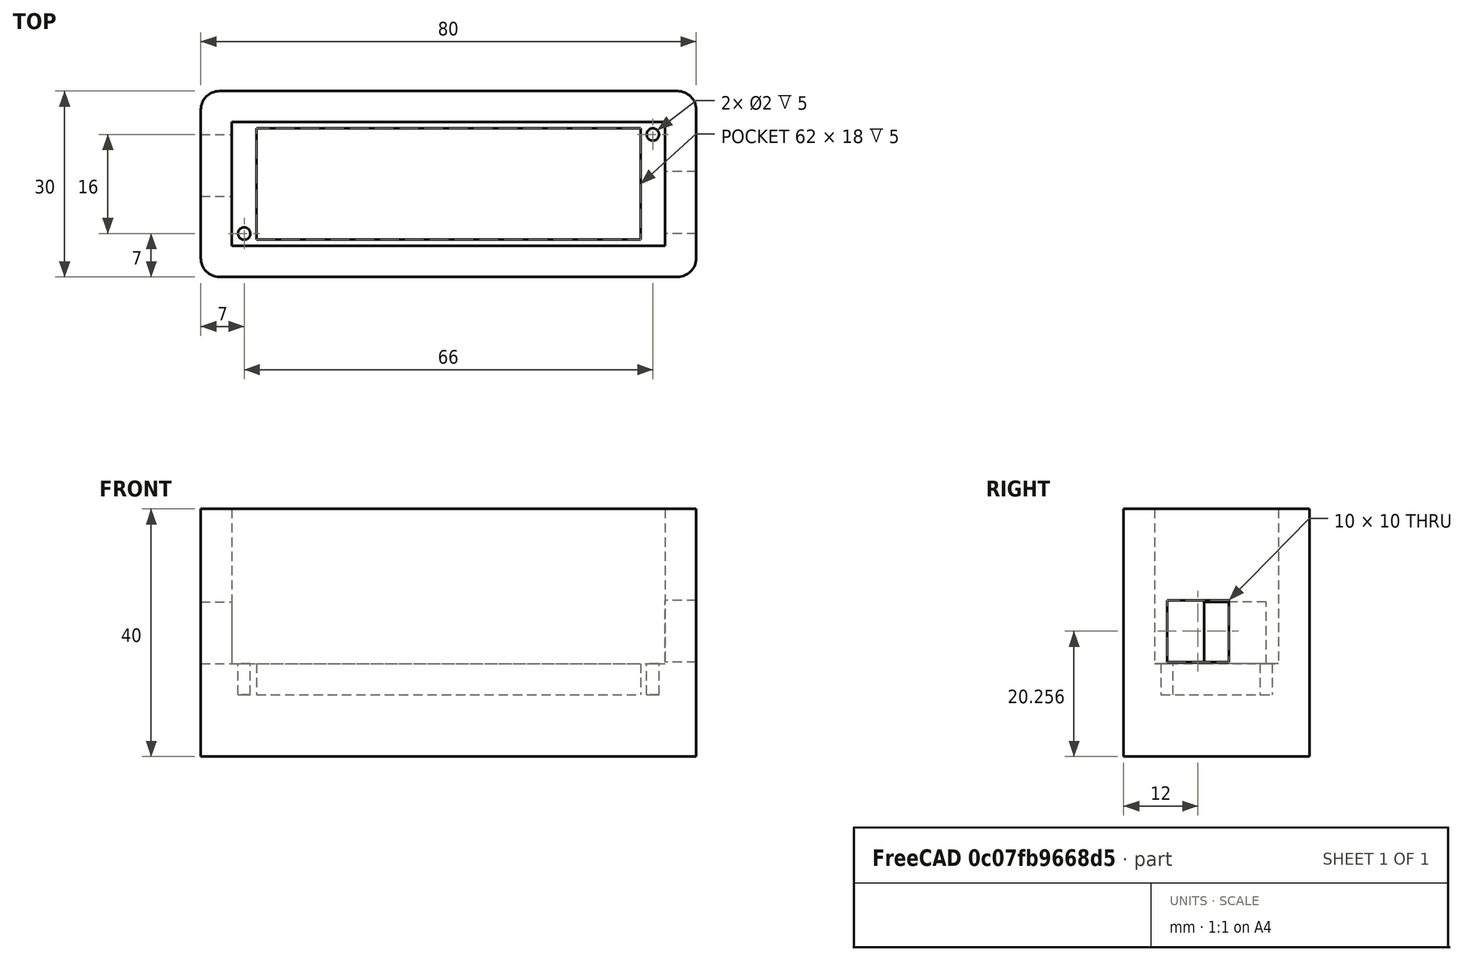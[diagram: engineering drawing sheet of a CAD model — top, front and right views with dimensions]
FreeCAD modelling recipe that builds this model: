
FCSTD DOCUMENT  (FreeCAD 0.20R29603 (Git))
Label: box
License: All rights reserved
LicenseURL: http://en.wikipedia.org/wiki/All_rights_reserved
objects: TechDraw::DrawViewDimension×41, Sketcher::SketchObject×6, PartDesign::Pocket×5, TechDraw::DrawViewSection×3, TechDraw::DrawViewPart×3, TechDraw::DrawSVGTemplate×2, TechDraw::DrawProjGroupItem×2, TechDraw::DrawPage×2, PartDesign::Pad×1, PartDesign::Fillet×1, TechDraw::DrawProjGroup×1, TechDraw::DrawViewDimExtent×1, PartDesign::Body×1
note: 21 computed .brp shape members not serialized (recipe doc carries the construction recipe); baked Part::Feature solids carry a one-line shape summary decoded from their .brp

FEATURE [TechDraw::DrawSVGTemplate] Template
  EditableTexts = Drawing_number=001; FC-SH=001; FC-Title=Box
  Height = 210
  Orientation = 1
  Width = 297
FEATURE [Sketcher::SketchObject] Sketch
  FullyConstrained = true
  MapMode = 5
  Placement = pos=(0,0,0) rot=(0.57735,0.57735,0.57735;2.0944rad)
  Support = -> [YZ_Plane]
  sketch-geometry (4):
    g0: LineSegment StartX=-30 StartY=40 StartZ=0 EndX=0 EndY=40 EndZ=0
    g1: LineSegment StartX=0 StartY=40 StartZ=0 EndX=0 EndY=0 EndZ=0
    g2: LineSegment StartX=0 StartY=0 StartZ=0 EndX=-30 EndY=0 EndZ=0
    g3: LineSegment StartX=-30 StartY=0 StartZ=0 EndX=-30 EndY=40 EndZ=0
  constraints (11):
    c: Coincident(g0,g1)
    c: Coincident(g1,g2)
    c: Coincident(g2,g3)
    c: Coincident(g3,g0)
    c: Horizontal(g0)
    c: Horizontal(g2)
    c: Vertical(g1)
    c: Vertical(g3)
    c: DistanceX(g2,g2) = 30
    c: DistanceY(g1,g1) = 40
    c: Coincident(g1,g-1)
FEATURE [PartDesign::Pad] Pad
  Direction = (1,-2e-16,3e-16)
  Length = 80
  Length2 = 10
  Midplane = true
  Placement = pos=(0,0,0) rot=(0.57735,0.57735,0.57735;2.0944rad)
  Profile = -> Sketch
  ReferenceAxis = -> Sketch [N_Axis]
  Type = 0
FEATURE [Sketcher::SketchObject] Sketch001
  ExternalGeometry = -> [Pad]
  FullyConstrained = true
  MapMode = 5
  Placement = pos=(-1.12e-14,1.76e-14,40) rot=(0,0,-1;1.5708rad)
  Support = -> [Pad]
  sketch-geometry (4):
    g0: LineSegment StartX=5 StartY=35 StartZ=0 EndX=25 EndY=35 EndZ=0
    g1: LineSegment StartX=25 StartY=35 StartZ=0 EndX=25 EndY=-35 EndZ=0
    g2: LineSegment StartX=25 StartY=-35 StartZ=0 EndX=5 EndY=-35 EndZ=0
    g3: LineSegment StartX=5 StartY=-35 StartZ=0 EndX=5 EndY=35 EndZ=0
  constraints (12):
    c: Coincident(g0,g1)
    c: Coincident(g1,g2)
    c: Coincident(g2,g3)
    c: Coincident(g3,g0)
    c: Horizontal(g0)
    c: Horizontal(g2)
    c: Vertical(g1)
    c: Vertical(g3)
    c: DistanceX(g2,g2) = 20
    c: DistanceY(g1,g1) = 70
    c: DistanceX(g1,g-3) = 5
    c: DistanceY(g-3,g1) = 5
FEATURE [PartDesign::Pocket] Pocket
  BaseFeature = -> Pad
  Direction = (4e-16,-6e-16,-1)
  Length = 25
  Length2 = 5
  Placement = pos=(0,0,0) rot=(0.57735,0.57735,0.57735;2.0944rad)
  Profile = -> Sketch001
  ReferenceAxis = -> Sketch001 [N_Axis]
  Type = 0
FEATURE [Sketcher::SketchObject] Sketch002
  ExternalGeometry = -> [Pocket]
  FullyConstrained = true
  MapMode = 5
  Placement = pos=(-6.1e-15,1.06e-14,15) rot=(0,0,-1;1.5708rad)
  Support = -> [Pocket]
  sketch-geometry (4):
    g0: LineSegment StartX=6 StartY=31 StartZ=0 EndX=24 EndY=31 EndZ=0
    g1: LineSegment StartX=24 StartY=31 StartZ=0 EndX=24 EndY=-31 EndZ=0
    g2: LineSegment StartX=24 StartY=-31 StartZ=0 EndX=6 EndY=-31 EndZ=0
    g3: LineSegment StartX=6 StartY=-31 StartZ=0 EndX=6 EndY=31 EndZ=0
  constraints (12):
    c: Coincident(g0,g1)
    c: Coincident(g1,g2)
    c: Coincident(g2,g3)
    c: Coincident(g3,g0)
    c: Horizontal(g0)
    c: Horizontal(g2)
    c: Vertical(g1)
    c: Vertical(g3)
    c: DistanceX(g2,g2) = 18
    c: DistanceY(g1,g1) = 62
    c: DistanceY(g-3,g1) = 4
    c: DistanceX(g1,g-3) = 1
FEATURE [PartDesign::Pocket] Pocket001
  BaseFeature = -> Pocket
  Direction = (7e-16,-8e-16,-1)
  Length = 5
  Length2 = 5
  Placement = pos=(0,0,0) rot=(0.57735,0.57735,0.57735;2.0944rad)
  Profile = -> Sketch002
  ReferenceAxis = -> Sketch002 [N_Axis]
  Type = 0
FEATURE [Sketcher::SketchObject] Sketch003
  ExternalGeometry = -> [Pocket001]
  FullyConstrained = true
  MapMode = 5
  Placement = pos=(-6.1e-15,1.06e-14,15) rot=(0,0,-1;1.5708rad)
  Support = -> [Pocket001]
  expr: Constraints[5] = 1 mm
  sketch-geometry (2):
    g0: Circle CenterX=7 CenterY=33 CenterZ=0 NormalX=0 NormalY=0 NormalZ=1 AngleXU=0 Radius=1
    g1: Circle CenterX=23 CenterY=-33 CenterZ=0 NormalX=0 NormalY=0 NormalZ=1 AngleXU=0 Radius=1
  constraints (6):
    c: DistanceX(g1,g-5) = 1
    c: DistanceY(g1,g-5) = 2
    c: DistanceX(g-6,g0) = 1
    c: DistanceY(g-6,g0) = 2
    c: Radius(g0) = 1
    c: Radius(g1) = 1
FEATURE [PartDesign::Pocket] Pocket002
  BaseFeature = -> Pocket001
  Direction = (1.1e-15,-9e-16,-1)
  Length = 5
  Length2 = 5
  Placement = pos=(0,0,0) rot=(0.57735,0.57735,0.57735;2.0944rad)
  Profile = -> Sketch003
  ReferenceAxis = -> Sketch003 [N_Axis]
  Type = 0
FEATURE [Sketcher::SketchObject] Sketch004
  ExternalGeometry = -> [Pocket002]
  FullyConstrained = true
  MapMode = 5
  Placement = pos=(-40,8.8e-15,-8.8e-15) rot=(0.57735,0.57735,-0.57735;4.18879rad)
  Support = -> [Pocket002]
  sketch-geometry (4):
    g0: LineSegment StartX=-17 StartY=-15 StartZ=0 EndX=-7 EndY=-15 EndZ=0
    g1: LineSegment StartX=-7 StartY=-15 StartZ=0 EndX=-7 EndY=-25 EndZ=0
    g2: LineSegment StartX=-7 StartY=-25 StartZ=0 EndX=-17 EndY=-25 EndZ=0
    g3: LineSegment StartX=-17 StartY=-25 StartZ=0 EndX=-17 EndY=-15 EndZ=0
  constraints (12):
    c: Coincident(g0,g1)
    c: Coincident(g1,g2)
    c: Coincident(g2,g3)
    c: Coincident(g3,g0)
    c: Horizontal(g0)
    c: Horizontal(g2)
    c: Vertical(g1)
    c: Vertical(g3)
    c: Equal(g1,g2)
    c: DistanceX(g2,g2) = 10
    c: DistanceX(g-3,g2) = 13
    c: DistanceY(g-3,g2) = 15
FEATURE [PartDesign::Pocket] Pocket003
  BaseFeature = -> Pocket002
  Direction = (1,-9e-16,8e-16)
  Length = 5
  Length2 = 5
  Placement = pos=(0,0,0) rot=(0.57735,0.57735,0.57735;2.0944rad)
  Profile = -> Sketch004
  ReferenceAxis = -> Sketch004 [N_Axis]
  Type = 0
FEATURE [Sketcher::SketchObject] Sketch005
  ExternalGeometry = -> [Pocket003]
  FullyConstrained = false
  MapMode = 5
  Placement = pos=(40,-9e-15,1.3e-14) rot=(0.57735,0.57735,0.57735;2.0944rad)
  sketch-geometry (4):
    g0: LineSegment StartX=-23 StartY=25.2559 StartZ=0 EndX=-13 EndY=25.2559 EndZ=0
    g1: LineSegment StartX=-13 StartY=25.2559 StartZ=0 EndX=-13 EndY=15.2559 EndZ=0
    g2: LineSegment StartX=-13 StartY=15.2559 StartZ=0 EndX=-23 EndY=15.2559 EndZ=0
    g3: LineSegment StartX=-23 StartY=15.2559 StartZ=0 EndX=-23 EndY=25.2559 EndZ=0
  constraints (11):
    c: Coincident(g0,g1)
    c: Coincident(g1,g2)
    c: Coincident(g2,g3)
    c: Coincident(g3,g0)
    c: Horizontal(g0)
    c: Horizontal(g2)
    c: Vertical(g1)
    c: Vertical(g3)
    c: DistanceX(g2,g2) = 10
    c: Equal(g2,g1)
    c: DistanceX(g-3,g0) = 7
FEATURE [PartDesign::Pocket] Pocket004
  BaseFeature = -> Pocket003
  Direction = (-1,0,0)
  Length = 5
  Length2 = 5
  Placement = pos=(0,0,0) rot=(0.57735,0.57735,0.57735;2.0944rad)
  Profile = -> Sketch005
  ReferenceAxis = -> Sketch005 [N_Axis]
  Type = 0
FEATURE [PartDesign::Fillet] Fillet
  Base = -> Pocket004 [Edge11,Edge18,Edge12,Edge10]
  BaseFeature = -> Pocket004
  Placement = pos=(0,0,0) rot=(0.57735,0.57735,0.57735;2.0944rad)
  Radius = 3
  SupportTransform = false
  UseAllEdges = false
FEATURE [TechDraw::DrawProjGroupItem] ProjItem  label="Front"
  CoarseView = false
  Direction = (0,-1,0)
  Focus = 100
  HardHidden = false
  IsoCount = 0
  IsoHidden = false
  IsoVisible = false
  LockPosition = true
  Perspective = false
  Rotation = 0
  RotationVector = (1,0,0)
  ScaleType = 2
  SeamHidden = false
  SeamVisible = true
  SmoothHidden = false
  SmoothVisible = true
  Source = -> [Fillet]
  Type = 0
  X = 0
  XDirection = (1,0,0)
  Y = 0
FEATURE [TechDraw::DrawProjGroupItem] ProjItem002  label="Top"
  CoarseView = false
  Direction = (0,0,1)
  Focus = 100
  HardHidden = false
  IsoCount = 0
  IsoHidden = false
  IsoVisible = false
  LockPosition = false
  Perspective = false
  Rotation = 0
  RotationVector = (1,0,0)
  ScaleType = 2
  SeamHidden = false
  SeamVisible = true
  SmoothHidden = false
  SmoothVisible = true
  Source = -> [Fillet]
  Type = 4
  X = 0
  XDirection = (1,0,0)
  Y = -70
FEATURE [TechDraw::DrawProjGroup] ProjGroup
  Anchor = -> ProjItem
  AutoDistribute = true
  LockPosition = false
  ProjectionType = 0
  Rotation = 0
  ScaleType = 0
  Source = -> [Fillet]
  Views = -> [ProjItem,ProjItem002]
  X = 82.0393
  Y = 156.709
  spacingX = 20
  spacingY = 30
FEATURE [TechDraw::DrawViewDimExtent] DimExtent
  AngleOverride = false
  Arbitrary = false
  ArbitraryTolerances = false
  CosmeticTags = d0a69e95-236e-45c1-b454-3df11a3e1382 | 03a514d8-6601-4757-9cdd-594276e1f8bd
  DirExtent = 0
  EqualTolerance = true
  ExtensionAngle = 0
  FormatSpec = %.2w
  FormatSpecOverTolerance = %+.2w
  FormatSpecUnderTolerance = %+.2w
  Inverted = false
  LineAngle = 0
  LockPosition = false
  MeasureType = 1
  OverTolerance = 0
  References2D = -> [ProjItem]
  Rotation = 0
  ScaleType = 0
  Source = -> [ProjItem]
  TheoreticalExact = false
  Type = 1
  UnderTolerance = 0
  X = 9.66102
  Y = 40.1695
FEATURE [TechDraw::DrawViewDimension] Dimension
  AngleOverride = false
  Arbitrary = false
  ArbitraryTolerances = false
  EqualTolerance = true
  ExtensionAngle = 0
  FormatSpec = %.2w
  FormatSpecOverTolerance = %+.2w
  FormatSpecUnderTolerance = %+.2w
  Inverted = false
  LineAngle = 0
  LockPosition = false
  MeasureType = 1
  OverTolerance = 0
  References2D = -> [ProjItem]
  Rotation = 0
  ScaleType = 0
  TheoreticalExact = false
  Type = 1
  UnderTolerance = 0
  X = 3.30509
  Y = 31.3983
FEATURE [TechDraw::DrawViewDimension] Dimension001
  AngleOverride = false
  Arbitrary = false
  ArbitraryTolerances = false
  EqualTolerance = true
  ExtensionAngle = 0
  FormatSpec = ⌀%.2w
  FormatSpecOverTolerance = %+.2w
  FormatSpecUnderTolerance = %+.2w
  Inverted = false
  LineAngle = 0
  LockPosition = false
  MeasureType = 1
  OverTolerance = 0
  References2D = -> [ProjItem002]
  Rotation = 0
  ScaleType = 0
  TheoreticalExact = false
  Type = 5
  UnderTolerance = 0
  X = -40.7762
  Y = 23.0474
FEATURE [TechDraw::DrawViewDimension] Dimension002
  AngleOverride = false
  Arbitrary = false
  ArbitraryTolerances = false
  EqualTolerance = true
  ExtensionAngle = 0
  FormatSpec = ⌀%.2w
  FormatSpecOverTolerance = %+.2w
  FormatSpecUnderTolerance = %+.2w
  Inverted = false
  LineAngle = 0
  LockPosition = false
  MeasureType = 1
  OverTolerance = 0
  References2D = -> [ProjItem002]
  Rotation = 0
  ScaleType = 0
  TheoreticalExact = false
  Type = 5
  UnderTolerance = 0
  X = 39.5116
  Y = 21.2814
FEATURE [TechDraw::DrawViewDimension] Dimension003
  AngleOverride = false
  Arbitrary = false
  ArbitraryTolerances = false
  EqualTolerance = true
  ExtensionAngle = 0
  FormatSpec = %.2w
  FormatSpecOverTolerance = %+.2w
  FormatSpecUnderTolerance = %+.2w
  Inverted = false
  LineAngle = 0
  LockPosition = false
  MeasureType = 1
  OverTolerance = 0
  References2D = -> [ProjItem002]
  Rotation = 0
  ScaleType = 0
  TheoreticalExact = false
  Type = 1
  UnderTolerance = 0
  X = 0.322341
  Y = 24.0713
FEATURE [TechDraw::DrawViewDimension] Dimension004
  AngleOverride = false
  Arbitrary = false
  ArbitraryTolerances = false
  EqualTolerance = true
  ExtensionAngle = 0
  FormatSpec = %.2w
  FormatSpecOverTolerance = %+.2w
  FormatSpecUnderTolerance = %+.2w
  Inverted = false
  LineAngle = 0
  LockPosition = false
  MeasureType = 1
  OverTolerance = 0
  References2D = -> [ProjItem002]
  Rotation = 0
  ScaleType = 0
  TheoreticalExact = false
  Type = 2
  UnderTolerance = 0
  X = -48.4102
  Y = 1.76436
FEATURE [TechDraw::DrawViewDimension] Dimension005
  AngleOverride = false
  Arbitrary = false
  ArbitraryTolerances = false
  EqualTolerance = true
  ExtensionAngle = 0
  FormatSpec = %.2w
  FormatSpecOverTolerance = %+.2w
  FormatSpecUnderTolerance = %+.2w
  Inverted = false
  LineAngle = 0
  LockPosition = false
  MeasureType = 1
  OverTolerance = 0
  References2D = -> [ProjItem002]
  Rotation = 0
  ScaleType = 0
  TheoreticalExact = false
  Type = 2
  UnderTolerance = 0
  X = -56.0884
  Y = 2.99043
FEATURE [TechDraw::DrawViewDimension] Dimension006
  AngleOverride = false
  Arbitrary = false
  ArbitraryTolerances = false
  EqualTolerance = true
  ExtensionAngle = 0
  FormatSpec = %.2w
  FormatSpecOverTolerance = %+.2w
  FormatSpecUnderTolerance = %+.2w
  Inverted = false
  LineAngle = 0
  LockPosition = false
  MeasureType = 1
  OverTolerance = 0
  References2D = -> [ProjItem002]
  Rotation = 0
  ScaleType = 0
  TheoreticalExact = false
  Type = 2
  UnderTolerance = 0
  X = -63.7283
  Y = 1.76436
FEATURE [TechDraw::DrawViewDimension] Dimension007
  AngleOverride = false
  Arbitrary = false
  ArbitraryTolerances = false
  EqualTolerance = true
  ExtensionAngle = 0
  FormatSpec = %.2w
  FormatSpecOverTolerance = %+.2w
  FormatSpecUnderTolerance = %+.2w
  Inverted = false
  LineAngle = 0
  LockPosition = false
  MeasureType = 1
  OverTolerance = 0
  References2D = -> [ProjItem002]
  Rotation = 0
  ScaleType = 0
  TheoreticalExact = false
  Type = 1
  UnderTolerance = 0
  X = -25.0018
  Y = -16.1668
FEATURE [TechDraw::DrawViewDimension] Dimension008
  AngleOverride = false
  Arbitrary = false
  ArbitraryTolerances = false
  EqualTolerance = true
  ExtensionAngle = 0
  FormatSpec = %.2w
  FormatSpecOverTolerance = %+.2w
  FormatSpecUnderTolerance = %+.2w
  Inverted = false
  LineAngle = 0
  LockPosition = false
  MeasureType = 1
  OverTolerance = 0
  References2D = -> [ProjItem002]
  Rotation = 0
  ScaleType = 0
  TheoreticalExact = false
  Type = 2
  UnderTolerance = 0
  X = 44.1572
  Y = 0.509573
FEATURE [TechDraw::DrawViewDimension] Dimension009
  AngleOverride = false
  Arbitrary = false
  ArbitraryTolerances = false
  EqualTolerance = true
  ExtensionAngle = 0
  FormatSpec = ⌀%.2w
  FormatSpecOverTolerance = %+.2w
  FormatSpecUnderTolerance = %+.2w
  Inverted = false
  LineAngle = 0
  LockPosition = false
  MeasureType = 1
  OverTolerance = 0
  References2D = -> [ProjItem002]
  Rotation = 0
  ScaleType = 0
  TheoreticalExact = false
  Type = 5
  UnderTolerance = 0
  X = -28.0769
  Y = 3.92341
FEATURE [TechDraw::DrawViewDimension] Dimension010
  AngleOverride = false
  Arbitrary = false
  ArbitraryTolerances = false
  EqualTolerance = true
  ExtensionAngle = 0
  FormatSpec = %.2w
  FormatSpecOverTolerance = %+.2w
  FormatSpecUnderTolerance = %+.2w
  Inverted = false
  LineAngle = 0
  LockPosition = false
  MeasureType = 1
  OverTolerance = 0
  References2D = -> [ProjItem]
  Rotation = 0
  ScaleType = 0
  TheoreticalExact = false
  Type = 2
  UnderTolerance = 0
  X = -51.9911
  Y = 1.72638
FEATURE [TechDraw::DrawViewSection] SectionView  label="Section  - "
  BaseView = -> ProjItem
  CoarseView = false
  CutSurfaceDisplay = 2
  Direction = (1,0,0)
  FileGeomPattern = <path>
  FileHatchPattern = <path>
  Focus = 100
  FuseBeforeCut = false
  HardHidden = false
  HatchScale = 1
  IsoCount = 0
  IsoHidden = false
  IsoVisible = false
  LockPosition = false
  NameGeomPattern = Diamond
  Perspective = false
  Rotation = 0
  ScaleType = 2
  SeamHidden = false
  SeamVisible = true
  SectionDirection = 1
  SectionNormal = (1,0,0)
  SectionOrigin = (-31,20,21)
  SmoothHidden = false
  SmoothVisible = true
  Source = -> [Fillet]
  X = 170
  XDirection = (0,1,0)
  Y = 156.737
FEATURE [TechDraw::DrawViewDimension] Dimension013
  AngleOverride = false
  Arbitrary = false
  ArbitraryTolerances = false
  EqualTolerance = true
  ExtensionAngle = 0
  FormatSpec = %.2w
  FormatSpecOverTolerance = %+.2w
  FormatSpecUnderTolerance = %+.2w
  Inverted = false
  LineAngle = 0
  LockPosition = false
  MeasureType = 1
  OverTolerance = 0
  References2D = -> [SectionView]
  Rotation = 0
  ScaleType = 0
  TheoreticalExact = false
  Type = 1
  UnderTolerance = 0
  X = 2.82345
  Y = 30.2754
FEATURE [TechDraw::DrawViewDimension] Dimension015
  AngleOverride = false
  Arbitrary = false
  ArbitraryTolerances = false
  EqualTolerance = true
  ExtensionAngle = 0
  FormatSpec = %.2w
  FormatSpecOverTolerance = %+.2w
  FormatSpecUnderTolerance = %+.2w
  Inverted = false
  LineAngle = 0
  LockPosition = false
  MeasureType = 1
  OverTolerance = 0
  References2D = -> [SectionView]
  Rotation = 0
  ScaleType = 0
  TheoreticalExact = false
  Type = 1
  UnderTolerance = 0
  X = 1.94209
  Y = 36.8008
FEATURE [TechDraw::DrawViewDimension] Dimension016
  AngleOverride = false
  Arbitrary = false
  ArbitraryTolerances = false
  EqualTolerance = true
  ExtensionAngle = 0
  FormatSpec = %.2w
  FormatSpecOverTolerance = %+.2w
  FormatSpecUnderTolerance = %+.2w
  Inverted = false
  LineAngle = 0
  LockPosition = false
  MeasureType = 1
  OverTolerance = 0
  References2D = -> [SectionView]
  Rotation = 0
  ScaleType = 0
  TheoreticalExact = false
  Type = 2
  UnderTolerance = 0
  X = 20.1822
  Y = 1.08757
FEATURE [TechDraw::DrawViewSection] SectionView001  label="Section  - 001"
  BaseView = -> ProjItem002
  CoarseView = false
  CutSurfaceDisplay = 2
  Direction = (1,0,0)
  FileGeomPattern = <path>
  FileHatchPattern = <path>
  Focus = 100
  FuseBeforeCut = false
  HardHidden = false
  HatchScale = 1
  IsoCount = 0
  IsoHidden = false
  IsoVisible = false
  LockPosition = false
  NameGeomPattern = Diamond
  Perspective = false
  Rotation = 0
  ScaleType = 2
  SeamHidden = false
  SeamVisible = true
  SectionDirection = 1
  SectionNormal = (1,0,0)
  SectionOrigin = (36,-15,20)
  SmoothHidden = false
  SmoothVisible = true
  Source = -> [Fillet]
  X = 170
  XDirection = (0,0,-1)
  Y = 86.3197
FEATURE [TechDraw::DrawViewDimension] Dimension017
  AngleOverride = false
  Arbitrary = false
  ArbitraryTolerances = false
  EqualTolerance = true
  ExtensionAngle = 0
  FormatSpec = %.2w
  FormatSpecOverTolerance = %+.2w
  FormatSpecUnderTolerance = %+.2w
  Inverted = false
  LineAngle = 0
  LockPosition = false
  MeasureType = 1
  OverTolerance = 0
  References2D = -> [SectionView001]
  Rotation = 0
  ScaleType = 0
  TheoreticalExact = false
  Type = 2
  UnderTolerance = 0
  X = -27.7754
  Y = 3.20621
FEATURE [TechDraw::DrawViewDimension] Dimension018
  AngleOverride = false
  Arbitrary = false
  ArbitraryTolerances = false
  EqualTolerance = true
  ExtensionAngle = 0
  FormatSpec = %.2w
  FormatSpecOverTolerance = %+.2w
  FormatSpecUnderTolerance = %+.2w
  Inverted = false
  LineAngle = 0
  LockPosition = false
  MeasureType = 1
  OverTolerance = 0
  References2D = -> [SectionView001]
  Rotation = 0
  ScaleType = 0
  TheoreticalExact = false
  Type = 2
  UnderTolerance = 0
  X = 26.4602
  Y = -1.38277
FEATURE [TechDraw::DrawViewDimension] Dimension019
  AngleOverride = false
  Arbitrary = false
  ArbitraryTolerances = false
  EqualTolerance = true
  ExtensionAngle = 0
  FormatSpec = %.2w
  FormatSpecOverTolerance = %+.2w
  FormatSpecUnderTolerance = %+.2w
  Inverted = false
  LineAngle = 0
  LockPosition = false
  MeasureType = 1
  OverTolerance = 0
  References2D = -> [SectionView001]
  Rotation = 0
  ScaleType = 0
  TheoreticalExact = false
  Type = 1
  UnderTolerance = 0
  X = -0.609006
  Y = 24.6271
FEATURE [TechDraw::DrawViewDimension] Dimension020
  AngleOverride = false
  Arbitrary = false
  ArbitraryTolerances = false
  EqualTolerance = true
  ExtensionAngle = 0
  FormatSpec = %.2w
  FormatSpecOverTolerance = %+.2w
  FormatSpecUnderTolerance = %+.2w
  Inverted = false
  LineAngle = 0
  LockPosition = false
  MeasureType = 1
  OverTolerance = 0
  References2D = -> [SectionView]
  Rotation = 0
  ScaleType = 0
  TheoreticalExact = false
  Type = 1
  UnderTolerance = 0
  X = 0
  Y = -21.7373
FEATURE [TechDraw::DrawViewDimension] Dimension021
  AngleOverride = false
  Arbitrary = false
  ArbitraryTolerances = false
  EqualTolerance = true
  ExtensionAngle = 0
  FormatSpec = %.2w
  FormatSpecOverTolerance = %+.2w
  FormatSpecUnderTolerance = %+.2w
  Inverted = false
  LineAngle = 0
  LockPosition = false
  MeasureType = 1
  OverTolerance = 0
  References2D = -> [SectionView]
  Rotation = 0
  ScaleType = 0
  TheoreticalExact = false
  Type = 2
  UnderTolerance = 0
  X = 20.1864
  Y = -11.3559
FEATURE [TechDraw::DrawViewDimension] Dimension022
  AngleOverride = false
  Arbitrary = false
  ArbitraryTolerances = false
  EqualTolerance = true
  ExtensionAngle = 0
  FormatSpec = %.2w
  FormatSpecOverTolerance = %+.2w
  FormatSpecUnderTolerance = %+.2w
  Inverted = false
  LineAngle = 0
  LockPosition = false
  MeasureType = 1
  OverTolerance = 0
  References2D = -> [SectionView]
  Rotation = 0
  ScaleType = 0
  TheoreticalExact = false
  Type = 2
  UnderTolerance = 0
  X = 30.5932
  Y = 8.72881
FEATURE [TechDraw::DrawPage] Page
  KeepUpdated = true
  NextBalloonIndex = 1
  ProjectionType = 0
  Template = -> Template
  Views = -> [ProjGroup,DimExtent,Dimension,Dimension001,Dimension002,Dimension003,Dimension004,Dimension005,Dimension006,Dimension007,Dimension008,Dimension009,Dimension010,SectionView,Dimension013,Dimension015,Dimension016,SectionView001,Dimension017,Dimension018,Dimension019,Dimension020,Dimension021,Dimension022]
FEATURE [PartDesign::Body] Body
  Group = -> [Sketch,Pad,Sketch001,Pocket,Sketch002,Pocket001,Sketch003,Pocket002,Sketch004,Sketch005,Pocket003,Pocket004,Fillet]
  Origin = -> Origin
  Tip = -> Fillet
FEATURE [TechDraw::DrawSVGTemplate] Template001
  EditableTexts = AUTHOR_NAME=Рєзнік О.С.; DRAWING_TITLE=ДЕ-91; FC-SC=1:1; FC-SH=2; FC-SI=A4; FreeCAD_DRAWING=Корпус для перетворювача напруги
  Height = 297
  Orientation = 0
  Width = 210
FEATURE [TechDraw::DrawViewPart] View
  CoarseView = false
  Direction = (1,0,0)
  Focus = 100
  HardHidden = false
  IsoCount = 0
  IsoHidden = false
  IsoVisible = false
  LockPosition = true
  Perspective = false
  Rotation = 0
  ScaleType = 0
  SeamHidden = false
  SeamVisible = true
  SmoothHidden = false
  SmoothVisible = true
  Source = -> [Fillet]
  X = 60
  XDirection = (0,1,0)
  Y = 240
FEATURE [TechDraw::DrawViewDimension] Dimension025
  AngleOverride = false
  Arbitrary = false
  ArbitraryTolerances = false
  EqualTolerance = true
  ExtensionAngle = 0
  FormatSpec = %.2w
  FormatSpecOverTolerance = %+.2w
  FormatSpecUnderTolerance = %+.2w
  Inverted = false
  LineAngle = 0
  LockPosition = false
  MeasureType = 1
  OverTolerance = 1
  References2D = -> [View]
  Rotation = 0
  ScaleType = 0
  TheoreticalExact = false
  Type = 2
  UnderTolerance = -1
  X = -29.9057
  Y = 2.14049
FEATURE [TechDraw::DrawViewDimension] Dimension026
  AngleOverride = false
  Arbitrary = false
  ArbitraryTolerances = false
  EqualTolerance = true
  ExtensionAngle = 0
  FormatSpec = %.2w
  FormatSpecOverTolerance = %+.2w
  FormatSpecUnderTolerance = %+.2w
  Inverted = false
  LineAngle = 0
  LockPosition = false
  MeasureType = 1
  OverTolerance = 0.5
  References2D = -> [View]
  Rotation = 0
  ScaleType = 0
  TheoreticalExact = false
  Type = 2
  UnderTolerance = -0.5
  X = -22.4084
  Y = -13.1684
FEATURE [TechDraw::DrawViewSection] SectionView002  label="Section А - А"
  BaseView = -> View
  CoarseView = false
  CutSurfaceDisplay = 2
  Direction = (0,1,0)
  FileGeomPattern = <path>
  FileHatchPattern = <path>
  Focus = 100
  FuseBeforeCut = false
  HardHidden = false
  HatchScale = 1
  IsoCount = 0
  IsoHidden = false
  IsoVisible = false
  LockPosition = true
  NameGeomPattern = Diamond
  Perspective = false
  Rotation = 0
  ScaleType = 0
  SeamHidden = false
  SeamVisible = true
  SectionDirection = 1
  SectionNormal = (0,1,0)
  SectionOrigin = (0,-7.1,23)
  SectionSymbol = А
  SmoothHidden = false
  SmoothVisible = true
  Source = -> [Fillet]
  X = 140
  XDirection = (-1,0,0)
  Y = 240
FEATURE [TechDraw::DrawViewDimension] Dimension030
  AngleOverride = false
  Arbitrary = false
  ArbitraryTolerances = false
  EqualTolerance = true
  ExtensionAngle = 0
  FormatSpec = %.2w
  FormatSpecOverTolerance = %+.2w
  FormatSpecUnderTolerance = %+.2w
  Inverted = false
  LineAngle = 0
  LockPosition = false
  MeasureType = 1
  OverTolerance = 0.5
  References2D = -> [SectionView002]
  Rotation = 0
  ScaleType = 0
  TheoreticalExact = false
  Type = 2
  UnderTolerance = -0.5
  X = 45.5536
  Y = -12.6547
FEATURE [TechDraw::DrawViewDimension] Dimension029
  AngleOverride = false
  Arbitrary = false
  ArbitraryTolerances = false
  EqualTolerance = true
  ExtensionAngle = 0
  FormatSpec = %.2w
  FormatSpecOverTolerance = %+.2w
  FormatSpecUnderTolerance = %+.2w
  Inverted = false
  LineAngle = 0
  LockPosition = false
  MeasureType = 1
  OverTolerance = 1
  References2D = -> [SectionView002]
  Rotation = 0
  ScaleType = 0
  TheoreticalExact = false
  Type = 1
  UnderTolerance = -1
  X = -23.5584
  Y = 38.6705
FEATURE [TechDraw::DrawViewDimension] Dimension028
  AngleOverride = false
  Arbitrary = false
  ArbitraryTolerances = false
  EqualTolerance = true
  ExtensionAngle = 0
  FormatSpec = %.2w
  FormatSpecOverTolerance = %+.2w
  FormatSpecUnderTolerance = %+.2w
  Inverted = false
  LineAngle = 0
  LockPosition = false
  MeasureType = 1
  OverTolerance = 0.5
  References2D = -> [SectionView002]
  Rotation = 0
  ScaleType = 0
  TheoreticalExact = false
  Type = 1
  UnderTolerance = -0.5
  X = -23.5906
  Y = 31.5664
FEATURE [TechDraw::DrawViewDimension] Dimension031
  AngleOverride = false
  Arbitrary = false
  ArbitraryTolerances = false
  EqualTolerance = true
  ExtensionAngle = 0
  FormatSpec = %.2w
  FormatSpecOverTolerance = %+.2w
  FormatSpecUnderTolerance = %+.2w
  Inverted = false
  LineAngle = 0
  LockPosition = false
  MeasureType = 1
  OverTolerance = 0.5
  References2D = -> [View]
  Rotation = 0
  ScaleType = 0
  TheoreticalExact = false
  Type = 1
  UnderTolerance = -0.5
  X = -20.5594
  Y = 40.6132
FEATURE [TechDraw::DrawViewPart] View002
  CoarseView = false
  Direction = (0.577,-0.577,0.577)
  Focus = 100
  HardHidden = false
  IsoCount = 0
  IsoHidden = false
  IsoVisible = false
  LockPosition = true
  Perspective = false
  Rotation = 0
  ScaleType = 0
  SeamHidden = false
  SeamVisible = true
  SmoothHidden = false
  SmoothVisible = true
  Source = -> [Body]
  X = 155
  XDirection = (0.707,0.707,0)
  Y = 120
FEATURE [TechDraw::DrawViewPart] View001
  CoarseView = false
  Direction = (0,0,1)
  Focus = 100
  HardHidden = false
  IsoCount = 0
  IsoHidden = false
  IsoVisible = false
  LockPosition = true
  Perspective = false
  Rotation = 0
  ScaleType = 0
  SeamHidden = false
  SeamVisible = true
  SmoothHidden = false
  SmoothVisible = true
  Source = -> [Body]
  X = 60
  XDirection = (0,1,0)
  Y = 140
FEATURE [TechDraw::DrawViewDimension] Dimension032
  AngleOverride = false
  Arbitrary = false
  ArbitraryTolerances = false
  EqualTolerance = true
  ExtensionAngle = 0
  FormatSpec = ⌀%.2w
  FormatSpecOverTolerance = %+.2w
  FormatSpecUnderTolerance = %+.2w
  Inverted = false
  LineAngle = 0
  LockPosition = false
  MeasureType = 1
  OverTolerance = 0
  References2D = -> [View001]
  Rotation = 0
  ScaleType = 0
  TheoreticalExact = false
  Type = 5
  UnderTolerance = 0
  X = 29.1574
  Y = 49.1767
FEATURE [TechDraw::DrawViewDimension] Dimension033
  AngleOverride = false
  Arbitrary = false
  ArbitraryTolerances = false
  EqualTolerance = true
  ExtensionAngle = 0
  FormatSpec = ⌀%.2w
  FormatSpecOverTolerance = %+.2w
  FormatSpecUnderTolerance = %+.2w
  Inverted = false
  LineAngle = 0
  LockPosition = false
  MeasureType = 1
  OverTolerance = 0
  References2D = -> [View001]
  Rotation = 0
  ScaleType = 0
  TheoreticalExact = false
  Type = 5
  UnderTolerance = 0
  X = 25.255
  Y = -39.9341
FEATURE [TechDraw::DrawViewDimension] Dimension034
  AngleOverride = false
  Arbitrary = false
  ArbitraryTolerances = false
  EqualTolerance = true
  ExtensionAngle = 0
  FormatSpec = %.2w
  FormatSpecOverTolerance = %+.2w
  FormatSpecUnderTolerance = %+.2w
  Inverted = false
  LineAngle = 0
  LockPosition = false
  MeasureType = 1
  OverTolerance = 0.5
  References2D = -> [View001]
  Rotation = 0
  ScaleType = 0
  TheoreticalExact = false
  Type = 2
  UnderTolerance = -0.5
  X = -26.0089
  Y = -1.56846
FEATURE [TechDraw::DrawViewDimension] Dimension035
  AngleOverride = false
  Arbitrary = false
  ArbitraryTolerances = false
  EqualTolerance = true
  ExtensionAngle = 0
  FormatSpec = %.2w
  FormatSpecOverTolerance = %+.2w
  FormatSpecUnderTolerance = %+.2w
  Inverted = false
  LineAngle = 0
  LockPosition = false
  MeasureType = 1
  OverTolerance = 0
  References2D = -> [View001]
  Rotation = 0
  ScaleType = 0
  TheoreticalExact = false
  Type = 2
  UnderTolerance = 0
  X = -26.0241
  Y = 39.2271
FEATURE [TechDraw::DrawViewDimension] Dimension036
  AngleOverride = false
  Arbitrary = false
  ArbitraryTolerances = false
  EqualTolerance = true
  ExtensionAngle = 0
  FormatSpec = %.2w
  FormatSpecOverTolerance = %+.2w
  FormatSpecUnderTolerance = %+.2w
  Inverted = false
  LineAngle = 0
  LockPosition = false
  MeasureType = 1
  OverTolerance = 0
  References2D = -> [View001]
  Rotation = 0
  ScaleType = 0
  TheoreticalExact = false
  Type = 1
  UnderTolerance = 0
  X = -2.57979
  Y = 49.3404
FEATURE [TechDraw::DrawViewDimension] Dimension037
  AngleOverride = false
  Arbitrary = false
  ArbitraryTolerances = false
  EqualTolerance = true
  ExtensionAngle = 0
  FormatSpec = %.2w
  FormatSpecOverTolerance = %+.2w
  FormatSpecUnderTolerance = %+.2w
  Inverted = false
  LineAngle = 0
  LockPosition = false
  MeasureType = 1
  OverTolerance = 0
  References2D = -> [SectionView002]
  Rotation = 0
  ScaleType = 0
  TheoreticalExact = false
  Type = 2
  UnderTolerance = 0
  X = -47.3324
  Y = -13.4954
FEATURE [TechDraw::DrawViewDimension] Dimension038
  AngleOverride = false
  Arbitrary = false
  ArbitraryTolerances = false
  EqualTolerance = true
  ExtensionAngle = 0
  FormatSpec = %.2w
  FormatSpecOverTolerance = %+.2w
  FormatSpecUnderTolerance = %+.2w
  Inverted = false
  LineAngle = 0
  LockPosition = false
  MeasureType = 1
  OverTolerance = 1
  References2D = -> [View001]
  Rotation = 0
  ScaleType = 0
  TheoreticalExact = false
  Type = 1
  UnderTolerance = -1
  X = -2.36069
  Y = -55.5904
FEATURE [TechDraw::DrawViewDimension] Dimension039
  AngleOverride = false
  Arbitrary = false
  ArbitraryTolerances = false
  EqualTolerance = true
  ExtensionAngle = 0
  FormatSpec = %.2w
  FormatSpecOverTolerance = %+.2w
  FormatSpecUnderTolerance = %+.2w
  Inverted = false
  LineAngle = 0
  LockPosition = false
  MeasureType = 1
  OverTolerance = 0.5
  References2D = -> [View001]
  Rotation = 0
  ScaleType = 0
  TheoreticalExact = false
  Type = 1
  UnderTolerance = -0.5
  X = -0.401383
  Y = -40.9247
FEATURE [TechDraw::DrawViewDimension] Dimension040
  AngleOverride = false
  Arbitrary = false
  ArbitraryTolerances = false
  EqualTolerance = true
  ExtensionAngle = 0
  FormatSpec = %.2w
  FormatSpecOverTolerance = %+.2w
  FormatSpecUnderTolerance = %+.2w
  Inverted = false
  LineAngle = 0
  LockPosition = false
  MeasureType = 1
  OverTolerance = 0.5
  References2D = -> [View001]
  Rotation = 0
  ScaleType = 0
  TheoreticalExact = false
  Type = 1
  UnderTolerance = -0.5
  X = 0.076511
  Y = -48.3367
FEATURE [TechDraw::DrawViewDimension] Dimension041
  AngleOverride = false
  Arbitrary = false
  ArbitraryTolerances = false
  EqualTolerance = true
  ExtensionAngle = 0
  FormatSpec = %.2w
  FormatSpecOverTolerance = %+.2w
  FormatSpecUnderTolerance = %+.2w
  Inverted = false
  LineAngle = 0
  LockPosition = false
  MeasureType = 1
  OverTolerance = 0.5
  References2D = -> [SectionView002]
  Rotation = 0
  ScaleType = 0
  TheoreticalExact = false
  Type = 1
  UnderTolerance = -0.5
  X = 50.4181
  Y = 31.5327
FEATURE [TechDraw::DrawViewDimension] Dimension042
  AngleOverride = false
  Arbitrary = false
  ArbitraryTolerances = false
  EqualTolerance = true
  ExtensionAngle = 0
  FormatSpec = %.2w
  FormatSpecOverTolerance = %+.2w
  FormatSpecUnderTolerance = %+.2w
  Inverted = false
  LineAngle = 0
  LockPosition = false
  MeasureType = 1
  OverTolerance = 0.5
  References2D = -> [View001]
  Rotation = 0
  ScaleType = 0
  TheoreticalExact = false
  Type = 1
  UnderTolerance = -0.5
  X = 26.9472
  Y = 56.3944
FEATURE [TechDraw::DrawViewDimension] Dimension043
  AngleOverride = false
  Arbitrary = false
  ArbitraryTolerances = false
  EqualTolerance = true
  ExtensionAngle = 0
  FormatSpec = %.2w
  FormatSpecOverTolerance = %+.2w
  FormatSpecUnderTolerance = %+.2w
  Inverted = false
  LineAngle = 0
  LockPosition = false
  MeasureType = 1
  OverTolerance = 0.5
  References2D = -> [SectionView002]
  Rotation = 0
  ScaleType = 0
  TheoreticalExact = false
  Type = 1
  UnderTolerance = -0.5
  X = -48.2753
  Y = 31.4518
FEATURE [TechDraw::DrawViewDimension] Dimension044
  AngleOverride = false
  Arbitrary = false
  ArbitraryTolerances = false
  EqualTolerance = true
  ExtensionAngle = 0
  FormatSpec = %.2w
  FormatSpecOverTolerance = %+.2w
  FormatSpecUnderTolerance = %+.2w
  Inverted = false
  LineAngle = 0
  LockPosition = false
  MeasureType = 1
  OverTolerance = 0.5
  References2D = -> [View001]
  Rotation = 0
  ScaleType = 0
  TheoreticalExact = false
  Type = 1
  UnderTolerance = -0.5
  X = -27.3657
  Y = 56.4623
FEATURE [TechDraw::DrawViewDimension] Dimension045
  AngleOverride = false
  Arbitrary = false
  ArbitraryTolerances = false
  EqualTolerance = true
  ExtensionAngle = 0
  FormatSpec = %.2w
  FormatSpecOverTolerance = %+.2w
  FormatSpecUnderTolerance = %+.2w
  Inverted = false
  LineAngle = 0
  LockPosition = false
  MeasureType = 1
  OverTolerance = 1
  References2D = -> [View001]
  Rotation = 0
  ScaleType = 0
  TheoreticalExact = false
  Type = 2
  UnderTolerance = -1
  X = -32.8836
  Y = -24.0131
FEATURE [TechDraw::DrawViewDimension] Dimension046
  AngleOverride = false
  Arbitrary = false
  ArbitraryTolerances = false
  EqualTolerance = true
  ExtensionAngle = 0
  FormatSpec = %.2w
  FormatSpecOverTolerance = %+.2w
  FormatSpecUnderTolerance = %+.2w
  Inverted = false
  LineAngle = 0
  LockPosition = false
  MeasureType = 1
  OverTolerance = 0
  References2D = -> [View]
  Rotation = 0
  ScaleType = 0
  TheoreticalExact = false
  Type = 1
  UnderTolerance = 0
  X = -5.44791
  Y = 31.9066
FEATURE [TechDraw::DrawPage] Page001
  KeepUpdated = false
  NextBalloonIndex = 1
  ProjectionType = 0
  Template = -> Template001
  Views = -> [View,SectionView002,View001,Dimension025,Dimension026,Dimension028,Dimension029,Dimension030,Dimension031,View002,Dimension032,Dimension033,Dimension034,Dimension035,Dimension036,Dimension037,Dimension038,Dimension039,Dimension040,Dimension041,Dimension042,Dimension043,Dimension044,Dimension045,Dimension046]
note: 6 file-system paths scrubbed to <path> (originals preserved in the JSON sidecar)
